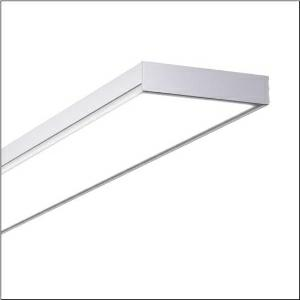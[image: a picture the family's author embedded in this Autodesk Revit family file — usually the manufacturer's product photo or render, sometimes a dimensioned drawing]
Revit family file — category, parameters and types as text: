
# Revit family: apollon_r__31_surface_51mp26wd2441ea_40fe
name_source: partatom
category: Lighting Fixtures
units: mm (PartAtom-declared; Revit-internal decimal feet)

## family parameters
Cut with Voids When Loaded = No
Host = Face
Light Source = No
Part Type = Normal
Room Calculation Point = No
Round Connector Dimension = Use Diameter
Shared = No

## types (1)
- Apollon® 31 Surface (1 x LED, 4600 lm, 33 W, 4000K)
    Apparent Load = 33 VA
    CIE Flux Codes = 61 87 97 97 100
    Color Rendering = 80
    Color Temperature = 4000K
    Default Elevation = 1800 mm
    Description = Apollon® 31 Surface, office luminaire, primary optical cover: micro prismatic cover, of PMMA, light emission: direct distribution, primary light characteristic: symmetric, installation type: surface-mounted, LED, rated luminous flux: 4.600lm, luminous efficacy: 139lm/W, light colour: 840, colour temperature: 4000K, control gear: DALI 2, with terminal, 5-pole, mains connection: 220..240V, AC, 50/60Hz, rated input power: 33W, housing, of sheet steel, coil coated, metallic grey (RAL 9006), length: 1.545mm, width: 200mm, height: 44mm, protection rating (complete): IP20, insulation class (complete): insulation class II (safety insulation), certification: CE, impact resistance: IK02, permissible operating ambient temperature: -20..+40°C, standard: EN 60598-2-22, packaging unit: 1 piece
    Height = 44 mm
    Lamp = 1 x LED
    Lamp Light Flux = 4600 lm
    Lamp Power = 33 W
    Lamp count = 1
    Length = 1545 mm
    Luminous efficacy = 139 lm/W
    Manufacturer = Siteco
    ModVariant = No
    Model = 51MP26WD2441EA
    Mounting Place = Ceiling
    Mounting Type = Surface mounted
    Number of Poles = 1
    OnlyDefault = Yes
    Power Factor = 1
    Product Name = Apollon® 31 Surface
    Product group = office luminaire | ceiling mounted
    ProductGroupID = 302
    Protection Class = Protection class II
    Protection Degree = IP 20
    RLX_Detail_Level = 1
    RLX_Emergency_Light_Flux = 0 lm
    RLX_Emergency_Type = 0
    RLX_Emergency_Type_DB = No
    RlxData = <blob elided: 24125 chars, md5=a2a2374e>
    Socket = socket
    Standby Power = 0 W
    System Light Flux = 4600 lm
    System Power = 33 W
    Type Comments = Product without accessories
    Type Image = l_1313654.jpg
    URL = http://relux.com
    VarID = ---
    Voltage = 0 V
    Weight = 0.00 kg
    Width = 200 mm  [stored 0.656168 ft]

note: [stored X ft] marks values corroborated as IEEE doubles in the binary element streams (Revit-internal decimal feet)

## geometry (parser evidence)
native form markers: Blend x4, Sweep x10
no freeform markers — native parametric forms only
